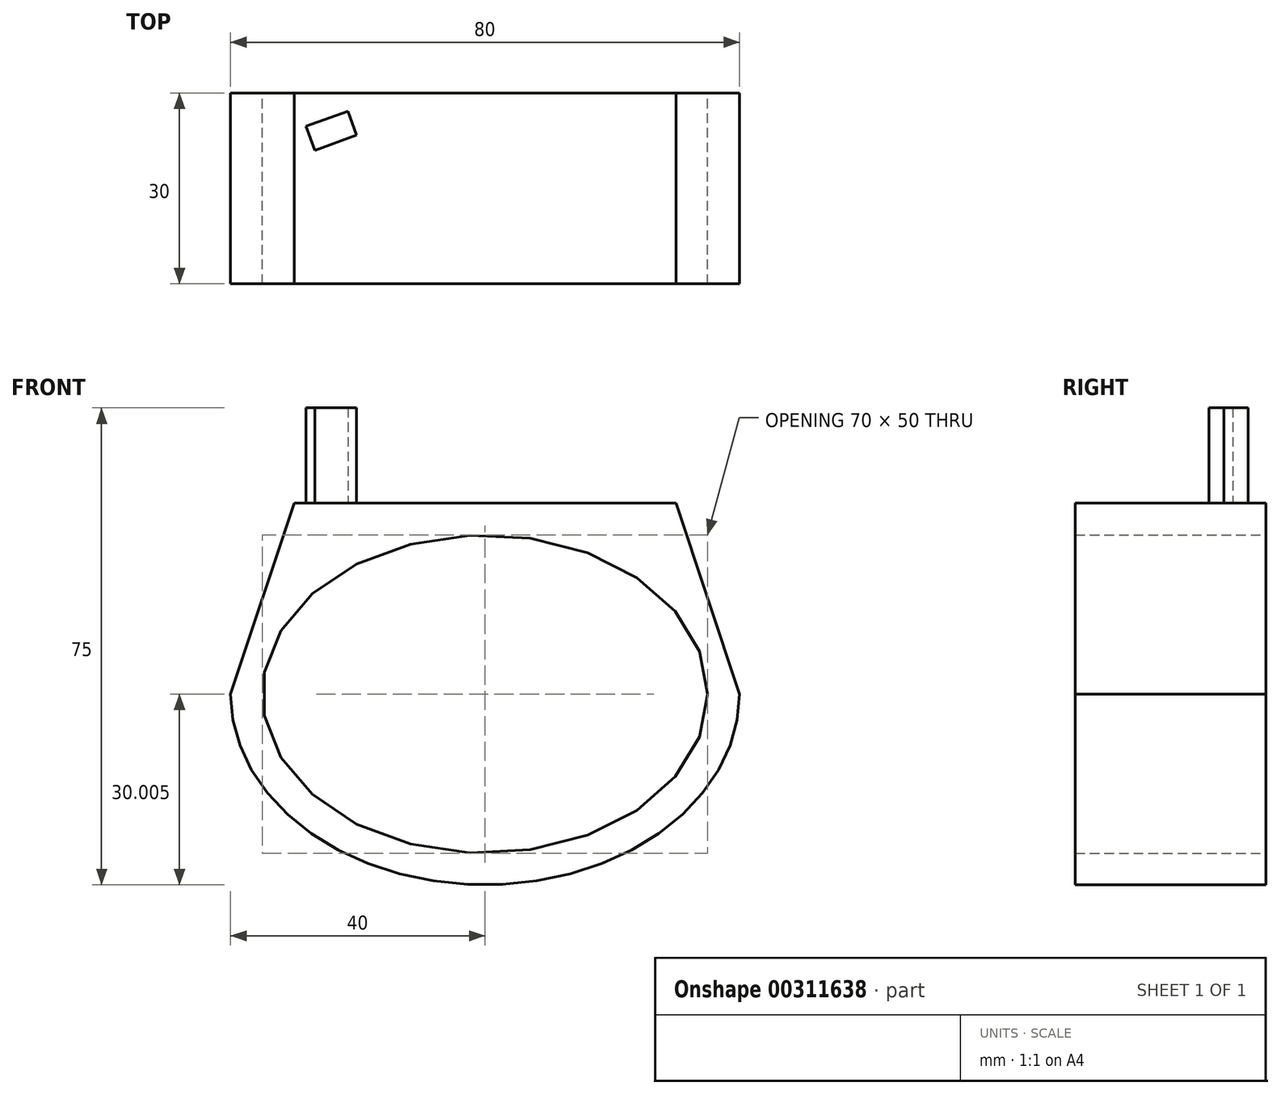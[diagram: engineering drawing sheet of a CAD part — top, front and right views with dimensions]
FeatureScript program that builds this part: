
annotation { "Feature Type Name" : "Feature", "Feature Type Description" : "" }
export const myFeature = defineFeature(function(context is Context, id is Id, definition is map)
    precondition{}
    {
        {
            var Q0;
            Q0=qCreatedBy(makeId("Front.planeOp"),FACE);
            var sketch = newSketch(context, id + "F0", { "sketchPlane" : qUnion([Q0])});
            skEllipse(sketch, "E0", {"center": v(-21.86, 10.75) * mm, "majorRadius": 35 * mm, "minorRadius": 25 * mm, "majorAxis": v(1, 0)});
            skLineSegment(sketch, "E1", {"start": v(-21.86, -14.25) * mm, "end": v(-21.86, 35.75) * mm, "construction": true});
            skLineSegment(sketch, "E2", {"start": v(-56.86, 10.75) * mm, "end": v(13.14, 10.75) * mm, "construction": true});
            skLineSegment(sketch, "E3", {"start": v(-21.86, 40.75) * mm, "end": v(-21.86, 35.75) * mm, "construction": true});
            skLineSegment(sketch, "E4", {"start": v(-21.86, -14.25) * mm, "end": v(-21.86, -19.25) * mm, "construction": true});
            skLineSegment(sketch, "E5", {"start": v(-56.86, 10.75) * mm, "end": v(-61.86, 10.75) * mm, "construction": true});
            skLineSegment(sketch, "E6", {"start": v(13.14, 10.75) * mm, "end": v(18.14, 10.75) * mm, "construction": true});
            skEllipticalArc(sketch, "E7", {});
            skLineSegment(sketch, "E8", {"start": v(-21.86, 40.75) * mm, "end": v(-21.86, 40.75) * mm});
            skLineSegment(sketch, "E9", {"start": v(-21.86, 40.75) * mm, "end": v(-51.86, 40.75) * mm});
            skLineSegment(sketch, "E10", {"start": v(-21.86, 40.75) * mm, "end": v(8.14, 40.75) * mm});
            skLineSegment(sketch, "E11", {"start": v(-51.86, 40.75) * mm, "end": v(-61.86, 10.75) * mm});
            skLineSegment(sketch, "E12", {"start": v(8.14, 40.75) * mm, "end": v(18.14, 10.75) * mm});
            const initialGuessF0  = {"E7": [-0.021859990432858467, 0.010754596441984177, 1, 0, 0.04, 0.03, 3.141592653589793, 0]};
            skSetInitialGuess(sketch, initialGuessF0);
            skSolve(sketch);
        }
        {
            var Q0;
            Q0=makeQuery(id+"F0.imprint","IMPRINT",FACE,{"disambiguationData":[TD([[makeQuery(id+"F0.imprint","IMPRINT",EDGE,{"derivedFrom":sQuery(id+"F0.wireOp",EDGE,"E0")}),-1.0]])]});
            extrude(context, id + "F1", {"entities" : qUnion([Q0]), "depth" : 30 * mm});
        }
        {
            var Q0;
            Q0=makeQuery(id+"F1.opExtrude","SWEPT_FACE",FACE,{"disambiguationData":[OSD([sQuery(id+"F0.wireOp",EDGE,"E9"),sQuery(id+"F0.wireOp",EDGE,"E10")])]});
            var sketch = newSketch(context, id + "F2", { "sketchPlane" : qUnion([Q0])});
            skLineSegment(sketch, "E13", {"start": v(-51.86, 0) * mm, "end": v(-51.86, -5.93) * mm});
            skLineSegment(sketch, "E14", {"start": v(-51.86, -5.93) * mm, "end": v(-43.4, -2.85) * mm});
            skLineSegment(sketch, "E15", {"start": v(-43.4, -2.85) * mm, "end": v(-42.03, -6.61) * mm});
            skLineSegment(sketch, "E16", {"start": v(-42.03, -6.61) * mm, "end": v(-48.61, -9) * mm});
            skLineSegment(sketch, "E17", {"start": v(-48.61, -9) * mm, "end": v(-49.98, -5.25) * mm});
            skSolve(sketch);
        }
        {
            var Q0;
            {var subQ0=sQuery(id+"F2.wireOp",EDGE,"E15");Q0=makeQuery(id+"F2.imprint","IMPRINT",FACE,{"disambiguationData":[TD([[makeQuery(id+"F2.imprint","IMPRINT",EDGE,{"derivedFrom":subQ0}),-1.0]])]});}
            extrude(context, id + "F3", {"entities" : qUnion([Q0]), "operationType" : NewBodyOperationType.ADD, "depth" : 15 * mm});
        }
    });
